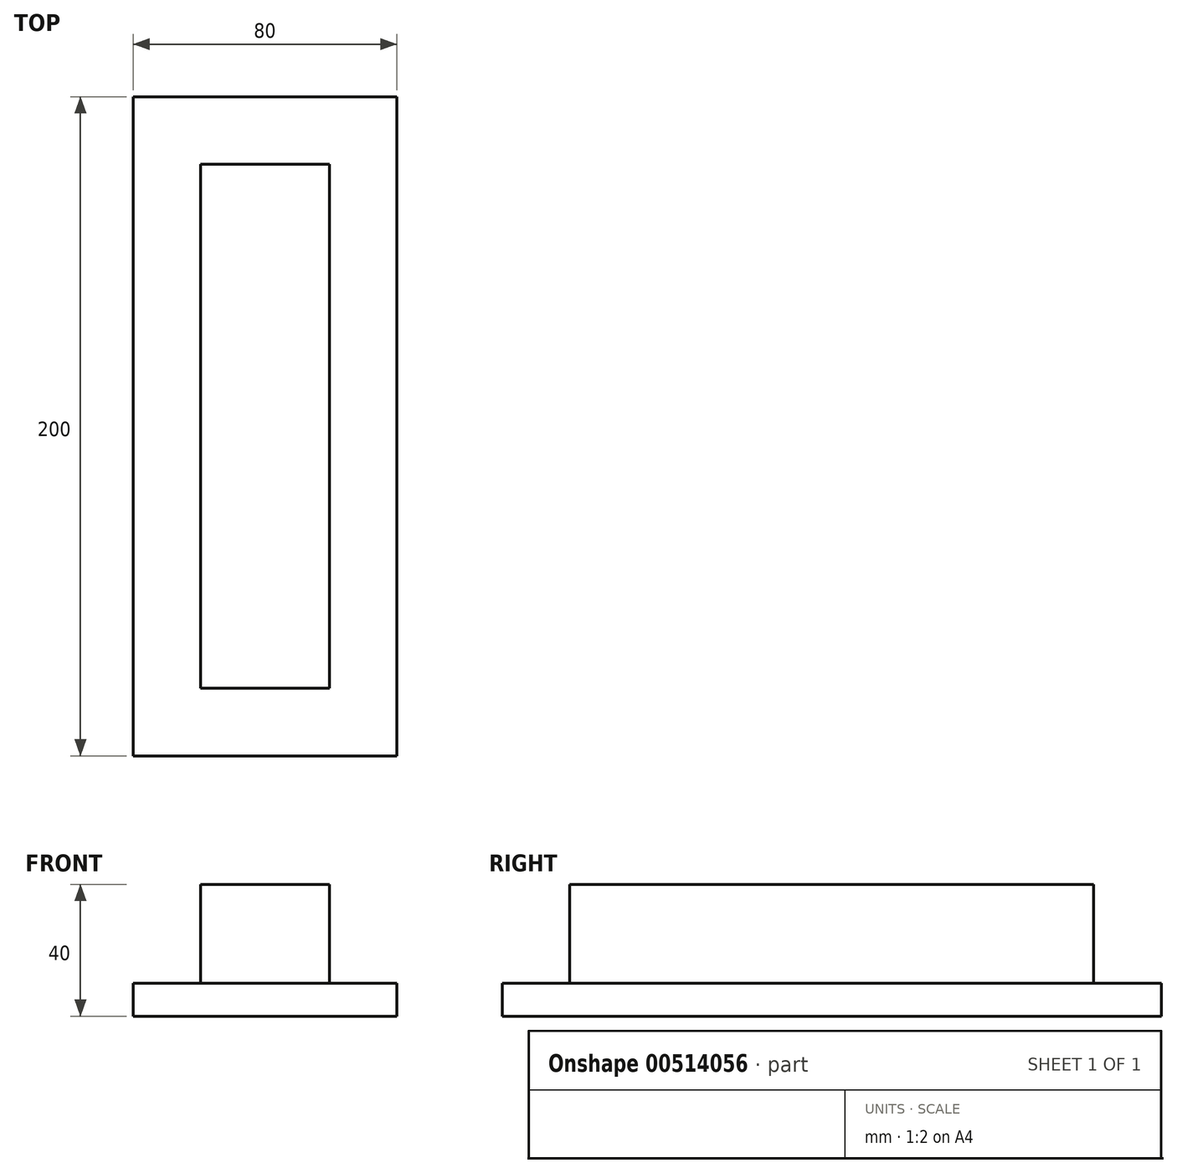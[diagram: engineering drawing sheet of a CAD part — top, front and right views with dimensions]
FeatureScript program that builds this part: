
annotation { "Feature Type Name" : "Feature", "Feature Type Description" : "" }
export const myFeature = defineFeature(function(context is Context, id is Id, definition is map)
    precondition{}
    {
        {
            var Q0;
            Q0=qCreatedBy(makeId("Top.planeOp"),FACE);
            var sketch = newSketch(context, id + "F0", { "sketchPlane" : qUnion([Q0])});
            skLineSegment(sketch, "E0.bottom", {"start": v(0, 0) * mm, "end": v(80, 0) * mm});
            skLineSegment(sketch, "E0.top", {"start": v(0, 200) * mm, "end": v(80, 200) * mm});
            skLineSegment(sketch, "E0.left", {"start": v(0, 0) * mm, "end": v(0, 200) * mm});
            skLineSegment(sketch, "E0.right", {"start": v(80, 0) * mm, "end": v(80, 200) * mm});
            skLineSegment(sketch, "E1.0", {"start": v(20.5, 179.5) * mm, "end": v(59.5, 179.5) * mm});
            skLineSegment(sketch, "E1.1", {"start": v(20.5, 20.5) * mm, "end": v(20.5, 179.5) * mm});
            skLineSegment(sketch, "E1.2", {"start": v(20.5, 20.5) * mm, "end": v(59.5, 20.5) * mm});
            skLineSegment(sketch, "E1.3", {"start": v(59.5, 20.5) * mm, "end": v(59.5, 179.5) * mm});
            skSolve(sketch);
        }
        {
            var Q0;
            Q0=qSketchRegion(id+"F0",true);
            var Q1;
            Q1=makeQuery(id+"F0.imprint","IMPRINT",FACE,{"disambiguationData":[TD([[makeQuery(id+"F0.imprint","IMPRINT",EDGE,{"derivedFrom":sQuery(id+"F0.wireOp",EDGE,"E0.bottom")}),1.0]])]});
            extrude(context, id + "F1", {"entities" : qUnion([Q0, Q1]), "depth" : 10 * mm});
        }
        {
            var Q0;
            Q0=makeQuery(id+"F0.imprint","IMPRINT",FACE,{"disambiguationData":[TD([[makeQuery(id+"F0.imprint","IMPRINT",EDGE,{"derivedFrom":sQuery(id+"F0.wireOp",EDGE,"E1.0")}),-1.0]])]});
            extrude(context, id + "F2", {"entities" : qUnion([Q0]), "operationType" : NewBodyOperationType.ADD, "depth" : 40 * mm});
        }
    });
